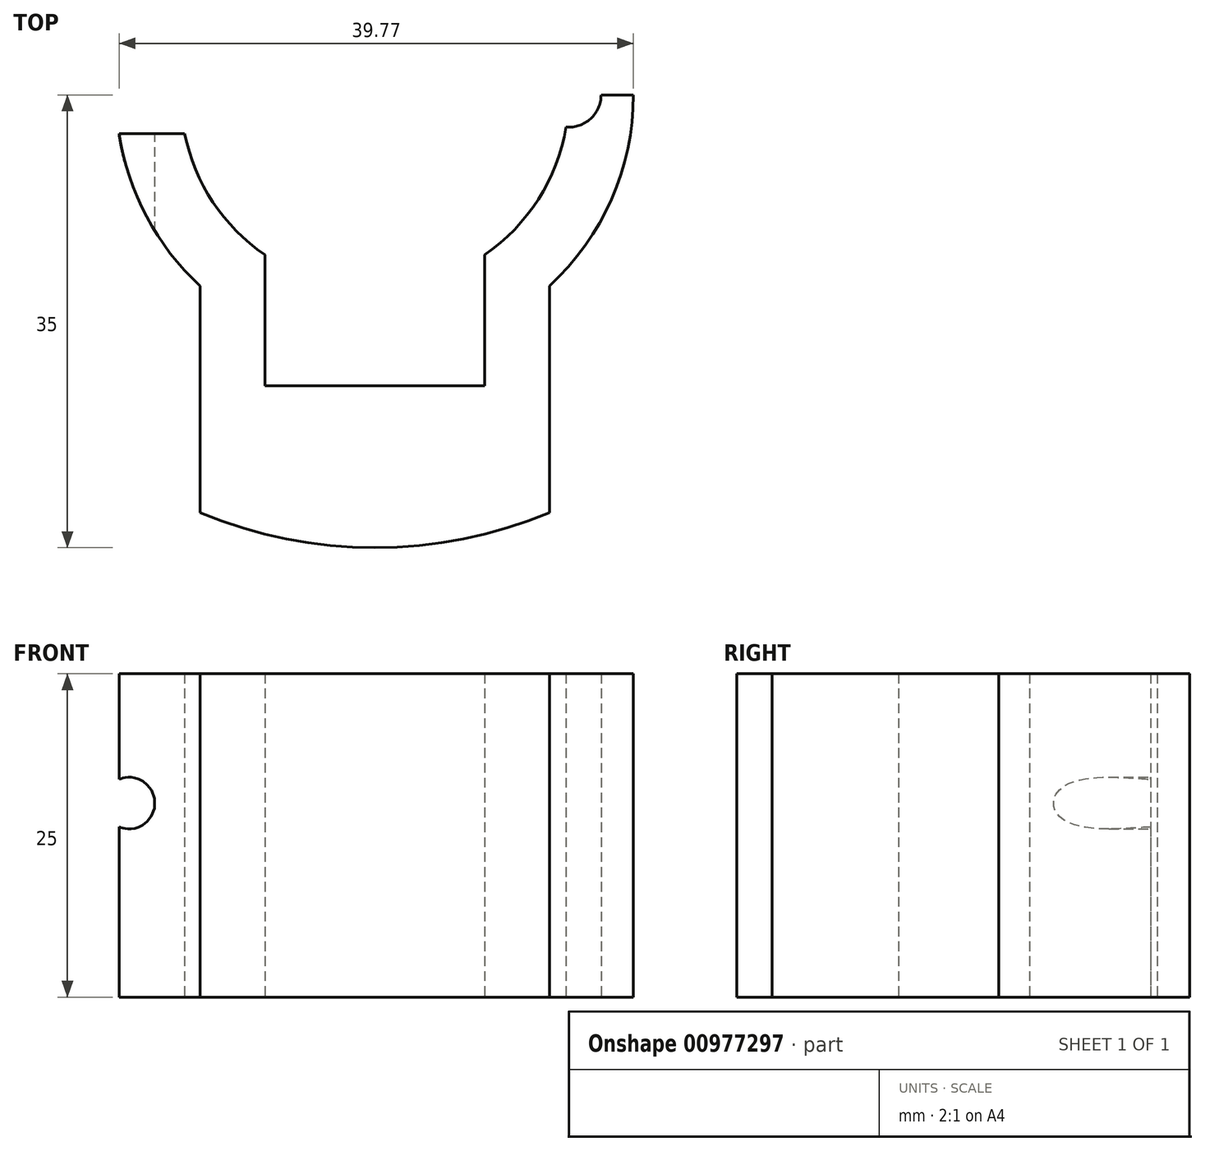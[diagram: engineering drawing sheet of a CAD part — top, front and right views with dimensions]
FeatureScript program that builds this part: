
annotation { "Feature Type Name" : "Feature", "Feature Type Description" : "" }
export const myFeature = defineFeature(function(context is Context, id is Id, definition is map)
    precondition{}
    {
        {
            var Q0;
            Q0=qCreatedBy(makeId("Top.planeOp"),FACE);
            var sketch = newSketch(context, id + "F0", { "sketchPlane" : qUnion([Q0])});
            skCircle(sketch, "E0", {"center": v(0, 0) * mm, "radius": 15 * mm});
            skLineSegment(sketch, "E1.bottom", {"start": v(-8.5, -22.5) * mm, "end": v(8.5, -22.5) * mm});
            skLineSegment(sketch, "E1.top", {"start": v(-8.5, -7.5) * mm, "end": v(8.5, -7.5) * mm});
            skLineSegment(sketch, "E1.left", {"start": v(-8.5, -22.5) * mm, "end": v(-8.5, -7.5) * mm});
            skLineSegment(sketch, "E1.right", {"start": v(8.5, -22.5) * mm, "end": v(8.5, -7.5) * mm});
            skPoint(sketch, "E1.middle", {"position": v(0, -15) * mm});
            skCircle(sketch, "E2", {"center": v(-4.5, -18.5) * mm, "radius": 2.5 * mm});
            skCircle(sketch, "E3", {"center": v(4.5, -18.5) * mm, "radius": 2.5 * mm});
            skCircle(sketch, "E4", {"center": v(0, 0) * mm, "radius": 35 * mm});
            skLineSegment(sketch, "E5", {"start": v(35, 0) * mm, "end": v(-35, 0) * mm});
            skCircle(sketch, "E6", {"center": v(0, 0) * mm, "radius": 20 * mm});
            skLineSegment(sketch, "E7", {"start": v(-13.5, -14.76) * mm, "end": v(-13.5, -32.3) * mm});
            skLineSegment(sketch, "E8", {"start": v(13.5, -14.76) * mm, "end": v(13.5, -32.3) * mm});
            skCircle(sketch, "E9", {"center": v(15, 0) * mm, "radius": 2.5 * mm});
            skLineSegment(sketch, "E10", {"start": v(-19.77, -3) * mm, "end": v(-14.7, -3) * mm});
            skSolve(sketch);
        }
        {
            var Q0;
            {var subQ5=sQuery(id+"F0.wireOp",EDGE,"E1.right");var subQ6=sQuery(id+"F0.wireOp",EDGE,"E0");var subQ7=makeQuery(id+"F0.imprint","INTERSECT",VERTEX,{"derivedFrom":[subQ6,subQ5]});Q0=makeQuery(id+"F0.imprint","IMPRINT",FACE,{"disambiguationData":[TD([[makeQuery(id+"F0.imprint","IMPRINT",EDGE,{"disambiguationData":[TD([[subQ7,-1.0]])],"derivedFrom":subQ6}),-1.0]])]});}
            var Q1;
            {var subQ6=sQuery(id+"F0.wireOp",EDGE,"E1.bottom");Q1=makeQuery(id+"F0.imprint","IMPRINT",FACE,{"disambiguationData":[TD([[makeQuery(id+"F0.imprint","IMPRINT",EDGE,{"derivedFrom":subQ6}),-1.0]])]});}
            var Q2;
            {var subQ2=sQuery(id+"F0.wireOp",EDGE,"E10");Q2=makeQuery(id+"F0.imprint","IMPRINT",FACE,{"disambiguationData":[TD([[makeQuery(id+"F0.imprint","IMPRINT",EDGE,{"derivedFrom":subQ2}),-1.0]])]});}
            extrude(context, id + "F1", {"entities" : qUnion([Q0, Q1, Q2]), "depth" : 25 * mm, "offsetDistance" : 25 * mm});
        }
        {
            var Q0;
            Q0=qCreatedBy(makeId("Front.planeOp"),FACE);
            var sketch = newSketch(context, id + "F2", { "sketchPlane" : qUnion([Q0])});
            skCircle(sketch, "E11", {"center": v(-19, 15) * mm, "radius": 2 * mm});
            skSolve(sketch);
        }
        {
            var Q0;
            Q0=qSketchRegion(id+"F2",true);
            extrude(context, id + "F3", {"entities" : qUnion([Q0]), "operationType" : NewBodyOperationType.REMOVE, "depth" : 25 * mm, "offsetDistance" : 25 * mm});
        }
    });
